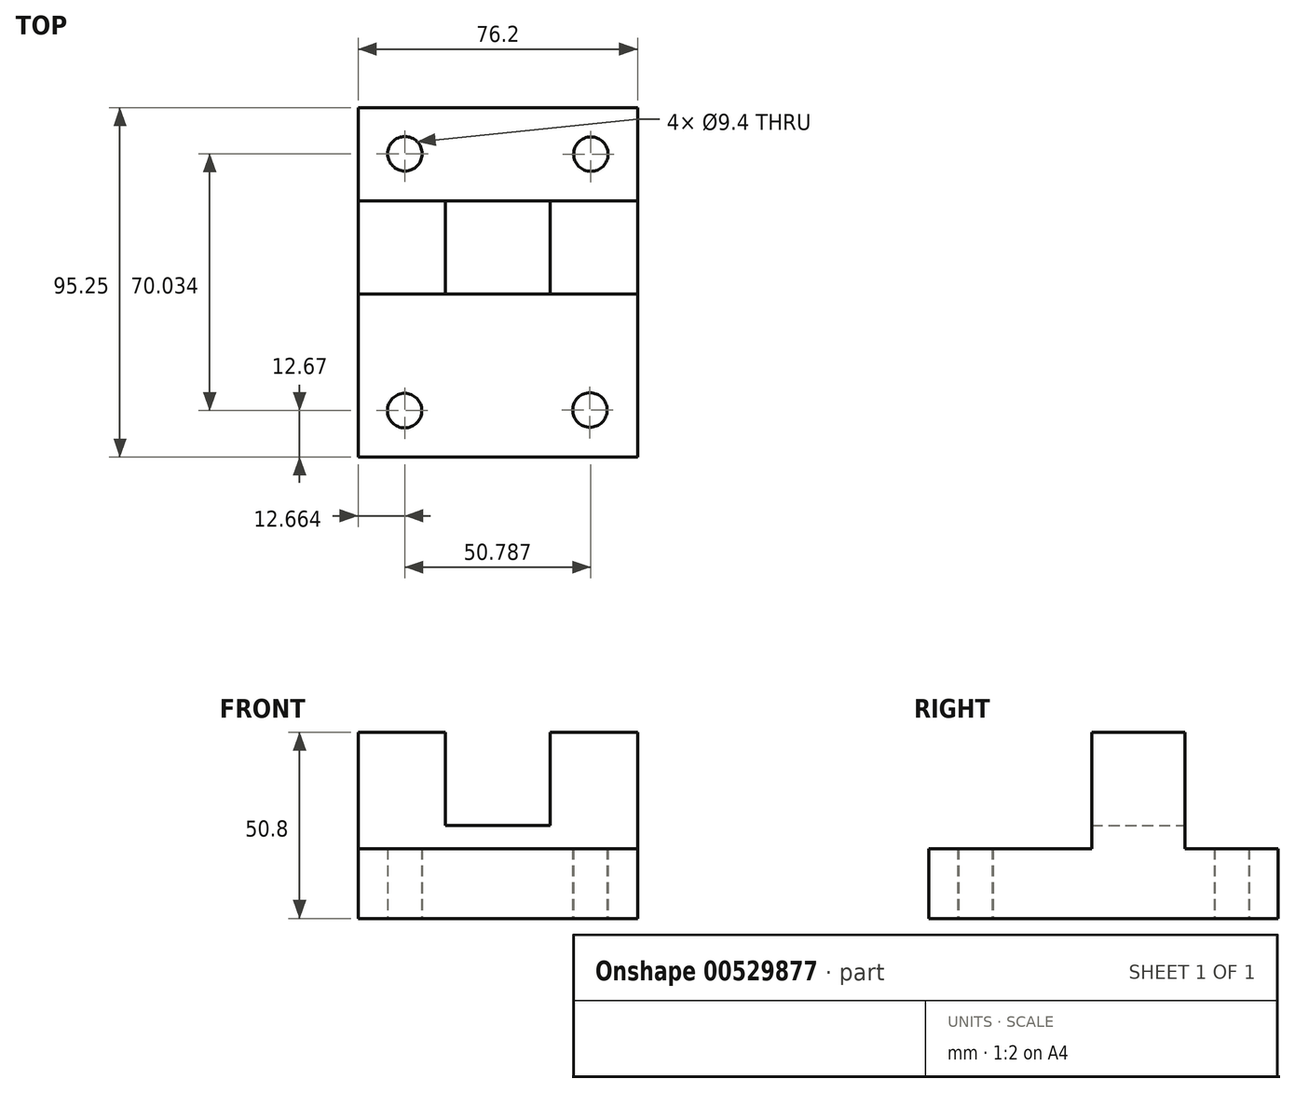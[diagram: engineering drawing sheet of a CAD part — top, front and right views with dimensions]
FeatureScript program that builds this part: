
annotation { "Feature Type Name" : "Feature", "Feature Type Description" : "" }
export const myFeature = defineFeature(function(context is Context, id is Id, definition is map)
    precondition{}
    {
        {
            var Q0;
            Q0=qCreatedBy(makeId("Top.planeOp"),FACE);
            var sketch = newSketch(context, id + "F0", { "sketchPlane" : qUnion([Q0])});
            skLineSegment(sketch, "E0", {"start": v(-30.14, 54.43) * mm, "end": v(-30.14, -40.82) * mm});
            skLineSegment(sketch, "E1", {"start": v(-30.14, -40.82) * mm, "end": v(46.06, -40.82) * mm});
            skLineSegment(sketch, "E2", {"start": v(46.06, -40.82) * mm, "end": v(46.06, 54.43) * mm});
            skLineSegment(sketch, "E3", {"start": v(46.06, 54.43) * mm, "end": v(-30.14, 54.43) * mm});
            skLineSegment(sketch, "E4", {"start": v(46.06, 29.03) * mm, "end": v(-30.14, 29.03) * mm});
            skLineSegment(sketch, "E5", {"start": v(46.06, -40.82) * mm, "end": v(46.06, 3.63) * mm});
            skLineSegment(sketch, "E6", {"start": v(46.06, 3.63) * mm, "end": v(-30.14, 3.63) * mm});
            skLineSegment(sketch, "E7", {"start": v(46.06, -40.82) * mm, "end": v(33.36, -40.82) * mm});
            skLineSegment(sketch, "E8", {"start": v(46.06, -40.82) * mm, "end": v(46.06, -28.12) * mm});
            skCircle(sketch, "E9", {"center": v(33.06, -28) * mm, "radius": 4.7 * mm});
            skCircle(sketch, "E10", {"center": v(-17.48, -28.15) * mm, "radius": 4.7 * mm});
            skLineSegment(sketch, "E11", {"start": v(-6.32, 16.65) * mm, "end": v(-6.32, 29.03) * mm});
            skLineSegment(sketch, "E12", {"start": v(-6.32, 29.03) * mm, "end": v(-6.32, 3.63) * mm});
            skPoint(sketch, "E13.orphan", {"position": v(-6.32, 0) * mm});
            skLineSegment(sketch, "E14", {"start": v(22.23, 18.12) * mm, "end": v(22.23, 29.03) * mm});
            skLineSegment(sketch, "E15", {"start": v(22.23, 29.03) * mm, "end": v(22.23, 3.63) * mm});
            skCircle(sketch, "E16", {"center": v(-17.4, 41.88) * mm, "radius": 4.7 * mm});
            skCircle(sketch, "E17", {"center": v(33.31, 41.78) * mm, "radius": 4.7 * mm});
            skLineSegment(sketch, "E18", {"start": v(-30.14, -40.82) * mm, "end": v(-30.14, -27.98) * mm});
            skLineSegment(sketch, "E19", {"start": v(-30.14, -40.82) * mm, "end": v(-17.44, -40.82) * mm});
            skLineSegment(sketch, "E20", {"start": v(-17.44, -40.82) * mm, "end": v(-23.8, -40.82) * mm});
            skLineSegment(sketch, "E21", {"start": v(-23.8, -40.82) * mm, "end": v(-21.76, -40.74) * mm});
            skPoint(sketch, "E22.orphan", {"position": v(-17.44, 52.4) * mm});
            skPoint(sketch, "E23.orphan", {"position": v(-17.44, 54.43) * mm});
            skPoint(sketch, "E24.end.orphan", {"position": v(33.36, 52.97) * mm});
            skPoint(sketch, "E25.start.orphan", {"position": v(33.36, 54.43) * mm});
            skSolve(sketch);
        }
        {
            var Q0;
            Q0 = qSketchRegion(id + "F0", true);
            extrude(context, id + "F1", {"entities" : qUnion([Q0]), "depth" : 19.05 * mm, "offsetDistance" : 25.4 * mm});
        }
        {
            var Q0;
            {var subQ0=sQuery(id+"F0.wireOp",EDGE,"E15");var subQ3=makeQuery(id+"F0.imprint","IMPRINT",VERTEX,{"derivedFrom":subQ0});Q0=makeQuery(id+"F0.imprint","IMPRINT",FACE,{"disambiguationData":[TD([[makeQuery(id+"F0.imprint","IMPRINT",EDGE,{"disambiguationData":[TD([[subQ3,1.0]])],"derivedFrom":subQ0}),1.0]])]});}
            var Q1;
            {var subQ0=sQuery(id+"F0.wireOp",EDGE,"E12");var subQ3=makeQuery(id+"F0.imprint","IMPRINT",VERTEX,{"derivedFrom":subQ0});Q1=makeQuery(id+"F0.imprint","IMPRINT",FACE,{"disambiguationData":[TD([[makeQuery(id+"F0.imprint","IMPRINT",EDGE,{"disambiguationData":[TD([[subQ3,1.0]])],"derivedFrom":subQ0}),-1.0]])]});}
            extrude(context, id + "F2", {"entities" : qUnion([Q0, Q1]), "operationType" : NewBodyOperationType.ADD, "depth" : 50.8 * mm, "offsetDistance" : 25.4 * mm});
        }
        {
            var Q0;
            {var subQ0=sQuery(id+"F0.wireOp",EDGE,"E12");var subQ3=makeQuery(id+"F0.imprint","IMPRINT",VERTEX,{"derivedFrom":subQ0});Q0=makeQuery(id+"F0.imprint","IMPRINT",FACE,{"disambiguationData":[TD([[makeQuery(id+"F0.imprint","IMPRINT",EDGE,{"disambiguationData":[TD([[subQ3,1.0]])],"derivedFrom":subQ0}),1.0]])]});}
            var Q1;
            Q1 = qSketchRegion(id + "F5", true);
            extrude(context, id + "F3", {"entities" : qUnion([Q0, Q1]), "operationType" : NewBodyOperationType.ADD, "depth" : 25.4 * mm, "offsetDistance" : 25.4 * mm});
        }
        {
            var Q0;
            {var subQ0=sQuery(id+"F0.wireOp",EDGE,"E12");var subQ3=makeQuery(id+"F0.imprint","IMPRINT",VERTEX,{"derivedFrom":subQ0});Q0=makeQuery(id+"F0.imprint","IMPRINT",FACE,{"disambiguationData":[TD([[makeQuery(id+"F0.imprint","IMPRINT",EDGE,{"disambiguationData":[TD([[subQ3,1.0]])],"derivedFrom":subQ0}),1.0]])]});}
            extrude(context, id + "F4", {"entities" : qUnion([Q0]), "operationType" : NewBodyOperationType.ADD, "depth" : 22.22 * mm, "offsetDistance" : 25.4 * mm});
        }
        {
            var Q0;
            Q0=makeQuery(id+"F1.opExtrude","SWEPT_FACE",FACE,{"disambiguationData":[OSD([sQuery(id+"F0.wireOp",EDGE,"E1"),sQuery(id+"F0.wireOp",EDGE,"E7"),sQuery(id+"F0.wireOp",EDGE,"E19"),sQuery(id+"F0.wireOp",EDGE,"E20")])]});
            var sketch = newSketch(context, id + "F5", { "sketchPlane" : qUnion([Q0])});
            skLineSegment(sketch, "E26", {"start": v(-30.14, 0) * mm, "end": v(46.06, 0) * mm});
            skLineSegment(sketch, "E27", {"start": v(46.06, 0) * mm, "end": v(46.06, 50.8) * mm});
            skPoint(sketch, "E27.endSnap0", {"position": v(46.06, 9.53) * mm});
            skLineSegment(sketch, "E28", {"start": v(46.06, 50.8) * mm, "end": v(22.23, 50.8) * mm});
            skLineSegment(sketch, "E29", {"start": v(22.23, 50.8) * mm, "end": v(22.23, 22.23) * mm});
            skLineSegment(sketch, "E30", {"start": v(22.23, 22.23) * mm, "end": v(-6.32, 22.23) * mm});
            skLineSegment(sketch, "E31", {"start": v(-6.32, 22.23) * mm, "end": v(-6.32, 50.8) * mm});
            skLineSegment(sketch, "E32", {"start": v(-6.32, 50.8) * mm, "end": v(-30.15, 50.8) * mm});
            skLineSegment(sketch, "E33", {"start": v(-30.15, 50.8) * mm, "end": v(-30.14, 0) * mm});
            skLineSegment(sketch, "E34", {"start": v(46.06, 0) * mm, "end": v(-30.14, 0) * mm});
            skSolve(sketch);
        }
        {
            var Q0;
            {var subQ0=sQuery(id+"F0.wireOp",EDGE,"E12");var subQ3=makeQuery(id+"F0.imprint","IMPRINT",VERTEX,{"derivedFrom":subQ0});Q0=makeQuery(id+"F0.imprint","IMPRINT",FACE,{"disambiguationData":[TD([[makeQuery(id+"F0.imprint","IMPRINT",EDGE,{"disambiguationData":[TD([[subQ3,1.0]])],"derivedFrom":subQ0}),1.0]])]});}
            extrude(context, id + "F6", {"entities" : qUnion([Q0]), "operationType" : NewBodyOperationType.ADD, "depth" : 22.22 * mm, "offsetDistance" : 25.4 * mm});
        }
    });
